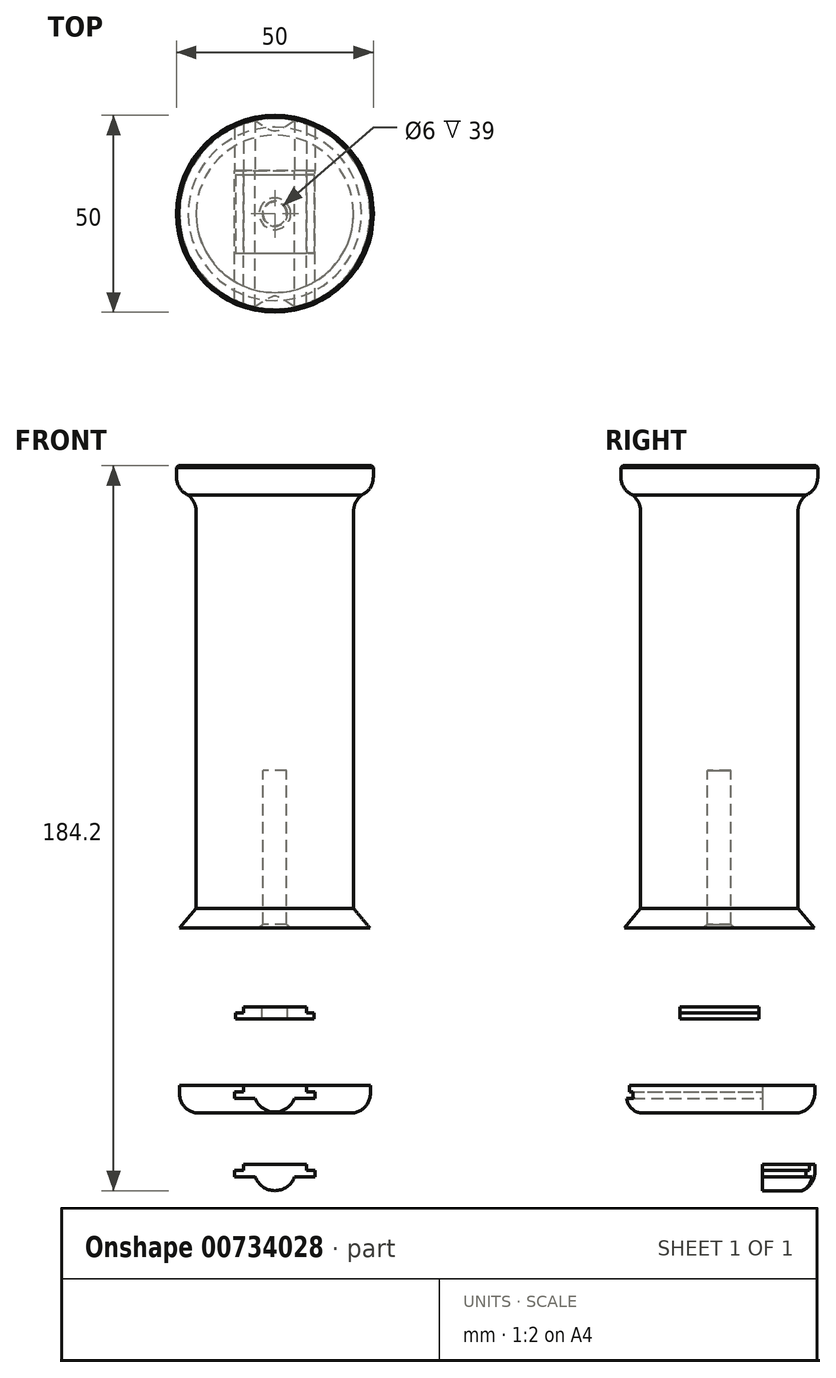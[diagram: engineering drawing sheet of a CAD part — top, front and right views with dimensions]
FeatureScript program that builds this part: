
annotation { "Feature Type Name" : "Feature", "Feature Type Description" : "" }
export const myFeature = defineFeature(function(context is Context, id is Id, definition is map)
    precondition{}
    {
        {
            var Q0;
            Q0=qCreatedBy(makeId("Front.planeOp"),FACE);
            var sketch = newSketch(context, id + "F0", { "sketchPlane" : qUnion([Q0])});
            skLineSegment(sketch, "E0", {"start": v(3, 0) * mm, "end": v(20, 0) * mm});
            skLineSegment(sketch, "E1", {"start": v(20, 0) * mm, "end": v(20, 110) * mm});
            skLineSegment(sketch, "E2", {"start": v(20, 110) * mm, "end": v(25, 110) * mm});
            skLineSegment(sketch, "E3", {"start": v(25, 110) * mm, "end": v(25, 117.5) * mm});
            skLineSegment(sketch, "E4", {"start": v(25, 117.5) * mm, "end": v(0, 117.5) * mm});
            skLineSegment(sketch, "E5", {"start": v(0, 117.5) * mm, "end": v(0, 40) * mm});
            skLineSegment(sketch, "E6", {"start": v(3, 0) * mm, "end": v(3, 40) * mm});
            skLineSegment(sketch, "E7", {"start": v(3, 40) * mm, "end": v(0, 40) * mm});
            skSolve(sketch);
        }
        {
            var Q0;
            Q0=makeQuery(id+"F0.imprint","IMPRINT",FACE,{"disambiguationData":[TD([[makeQuery(id+"F0.imprint","IMPRINT",EDGE,{"derivedFrom":sQuery(id+"F0.wireOp",EDGE,"E0")}),1.0]])]});
            var Q1;
            Q1=sQuery(id+"F0.wireOp",EDGE,"E5");
            revolve(context, id + "F1", {"surfaceOperationType" : NewSurfaceOperationType.NEW, "entities" : qUnion([Q0]), "axis" : qUnion([Q1]), "revolveType" : RevolveType.FULL});
        }
        {
            var Q0;
            Q0=makeQuery(id+"F1.opRevolve","SWEPT_EDGE",EDGE,{"disambiguationData":[OSD([sQuery(id+"F0.wireOp",EDGE,"E1"),sQuery(id+"F0.wireOp",EDGE,"E2")])]});
            chamfer(context, id + "F2", {"entities" : qUnion([Q0]), "width" : 2 * mm, "tangentPropagation" : true});
        }
        {
            var Q0;
            {var subQ0=sQuery(id+"F0.wireOp",EDGE,"E1");Q0=makeQuery(id+"F2.opChamfer","BLEND_EDGE",EDGE,{"blendedFrom":[makeQuery(id+"F1.opRevolve","SWEPT_EDGE",EDGE,{"disambiguationData":[OSD([subQ0,sQuery(id+"F0.wireOp",EDGE,"E2")])]}),makeQuery(id+"F1.opRevolve","SWEPT_FACE",FACE,{"disambiguationData":[OSD([subQ0])]})],"blendedInto":[makeQuery(id+"F1.opRevolve","SWEPT_FACE",FACE,{"disambiguationData":[OSD([subQ0])]})]});}
            var Q1;
            Q1=makeQuery(id+"F1.opRevolve","SWEPT_EDGE",EDGE,{"disambiguationData":[OSD([sQuery(id+"F0.wireOp",EDGE,"E2"),sQuery(id+"F0.wireOp",EDGE,"E3")])]});
            fillet(context, id + "F3", {"entities" : qUnion([Q0, Q1]), "radius" : 5 * mm, "tangentPropagation" : true, "allowEdgeOverflow" : false});
        }
        {
            var Q0;
            Q0=makeQuery(id+"F1.opRevolve","SWEPT_EDGE",EDGE,{"disambiguationData":[OSD([sQuery(id+"F0.wireOp",EDGE,"E0"),sQuery(id+"F0.wireOp",EDGE,"E6")])]});
            chamfer(context, id + "F4", {"entities" : qUnion([Q0]), "width" : 1 * mm, "tangentPropagation" : true});
        }
        {
            var Q0;
            Q0=makeQuery(id+"F1.opRevolve","SWEPT_EDGE",EDGE,{"disambiguationData":[OSD([sQuery(id+"F0.wireOp",EDGE,"E3"),sQuery(id+"F0.wireOp",EDGE,"E4")])]});
            chamfer(context, id + "F5", {"entities" : qUnion([Q0]), "width" : 0.5 * mm, "tangentPropagation" : true});
        }
        {
            var Q0;
            Q0=qCreatedBy(makeId("Top.planeOp"),FACE);
            var sketch = newSketch(context, id + "F6", { "sketchPlane" : qUnion([Q0])});
            skCircle(sketch, "E8", {"center": v(0, 0) * mm, "radius": 25 * mm});
            skCircle(sketch, "E9", {"center": v(0, 0) * mm, "radius": 20 * mm});
            skSolve(sketch);
        }
        {
            var Q0;
            Q0 = qSketchRegion(id + "F6", true);
            extrude(context, id + "F7", {"entities" : qUnion([Q0]), "operationType" : NewBodyOperationType.ADD, "depth" : 5 * mm, "offsetDistance" : 25 * mm});
        }
        {
            var Q0;
            Q0=makeQuery(id+"F7.opExtrude","CAP_EDGE",EDGE,{"disambiguationData":[OSD([sQuery(id+"F6.wireOp",EDGE,"E8")])],"isStart":false});
            chamfer(context, id + "F8", {"entities" : qUnion([Q0]), "chamferType" : ChamferType.TWO_OFFSETS, "width1" : 5 * mm, "oppositeDirection" : false, "width2" : 6 * mm, "tangentPropagation" : true});
        }
        {
            var Q0;
            Q0=qCreatedBy(makeId("Top.planeOp"),FACE);
            cPlane(context, id + "F9", {"entities" : qUnion([Q0]), "cplaneType" : CPlaneType.OFFSET, "offset" : 20 * mm, "oppositeDirection" : true, "width" : 150 * mm, "height" : 150 * mm});
        }
        {
            var Q0;
            Q0=qCreatedBy(id+"F9.planeOp",FACE);
            var sketch = newSketch(context, id + "F10", { "sketchPlane" : qUnion([Q0])});
            skCircle(sketch, "E10", {"center": v(0, 0) * mm, "radius": 3.2 * mm});
            skLineSegment(sketch, "E11.bottom", {"start": v(-10, -10) * mm, "end": v(10, -10) * mm});
            skLineSegment(sketch, "E11.top", {"start": v(-10, 10) * mm, "end": v(10, 10) * mm});
            skLineSegment(sketch, "E11.left", {"start": v(-10, -10) * mm, "end": v(-10, 10) * mm});
            skLineSegment(sketch, "E11.right", {"start": v(10, -10) * mm, "end": v(10, 10) * mm});
            skSolve(sketch);
        }
        {
            var Q0;
            Q0=makeQuery(id+"F10.imprint","IMPRINT",FACE,{"disambiguationData":[TD([[makeQuery(id+"F10.imprint","IMPRINT",EDGE,{"derivedFrom":sQuery(id+"F10.wireOp",EDGE,"E10")}),-1.0]])]});
            extrude(context, id + "F11", {"entities" : qUnion([Q0]), "oppositeDirection" : true, "depth" : 3 * mm, "offsetDistance" : 25 * mm});
        }
        {
            var Q0;
            Q0=qCreatedBy(makeId("Front.planeOp"),FACE);
            var sketch = newSketch(context, id + "F12", { "sketchPlane" : qUnion([Q0])});
            skLineSegment(sketch, "E12.bottom", {"start": v(-10, -20) * mm, "end": v(-8, -20) * mm});
            skLineSegment(sketch, "E12.top", {"start": v(-10, -21.5) * mm, "end": v(-8, -21.5) * mm});
            skLineSegment(sketch, "E12.left", {"start": v(-10, -20) * mm, "end": v(-10, -21.5) * mm});
            skLineSegment(sketch, "E12.right", {"start": v(-8, -20) * mm, "end": v(-8, -21.5) * mm});
            skLineSegment(sketch, "E13", {"start": v(0, -22.98) * mm, "end": v(0, -19.98) * mm});
            skLineSegment(sketch, "E14.MirrorCS", {"start": v(10, -20) * mm, "end": v(10, -21.5) * mm});
            skLineSegment(sketch, "E15.MirrorCS", {"start": v(10, -21.5) * mm, "end": v(8, -21.5) * mm});
            skLineSegment(sketch, "E16.MirrorCS", {"start": v(8, -20) * mm, "end": v(8, -21.5) * mm});
            skLineSegment(sketch, "E17.MirrorCS", {"start": v(10, -20) * mm, "end": v(8, -20) * mm});
            skSolve(sketch);
        }
        {
            var Q0;
            Q0 = qSketchRegion(id + "F12", true);
            extrude(context, id + "F13", {"entities" : qUnion([Q0]), "operationType" : NewBodyOperationType.REMOVE, "endBound" : BoundingType.SYMMETRIC, "oppositeDirection" : true, "depth" : 20 * mm, "offsetDistance" : 25 * mm});
        }
        {
            var Q0;
            Q0=qCreatedBy(id+"F9.planeOp",FACE);
            cPlane(context, id + "F14", {"entities" : qUnion([Q0]), "cplaneType" : CPlaneType.OFFSET, "offset" : 20 * mm, "oppositeDirection" : true, "width" : 150 * mm, "height" : 150 * mm});
        }
        {
            var Q0;
            Q0=qCreatedBy(id+"F14.planeOp",FACE);
            var sketch = newSketch(context, id + "F15", { "sketchPlane" : qUnion([Q0])});
            skCircle(sketch, "E18", {"center": v(0, 0) * mm, "radius": 24.25 * mm});
            skSolve(sketch);
        }
        {
            var Q0;
            Q0=makeQuery(id+"F15.imprint","IMPRINT",FACE,{"disambiguationData":[TD([[makeQuery(id+"F15.imprint","IMPRINT",EDGE,{"derivedFrom":sQuery(id+"F15.wireOp",EDGE,"E18")}),1.0]])]});
            extrude(context, id + "F16", {"entities" : qUnion([Q0]), "oppositeDirection" : true, "depth" : 7 * mm, "offsetDistance" : 25 * mm});
        }
        {
            var Q0;
            Q0=makeQuery(id+"F16.opExtrude","CAP_EDGE",EDGE,{"disambiguationData":[OSD([sQuery(id+"F15.wireOp",EDGE,"E18")])],"isStart":false});
            fillet(context, id + "F17", {"entities" : qUnion([Q0]), "radius" : 5 * mm, "tangentPropagation" : true, "allowEdgeOverflow" : false});
        }
        {
            var Q0;
            Q0=qCreatedBy(makeId("Front.planeOp"),FACE);
            var sketch = newSketch(context, id + "F18", { "sketchPlane" : qUnion([Q0])});
            skLineSegment(sketch, "E19", {"start": v(0, -40) * mm, "end": v(-8, -40) * mm});
            skLineSegment(sketch, "E20", {"start": v(-8, -40) * mm, "end": v(-8, -41.6) * mm});
            skLineSegment(sketch, "E21", {"start": v(-8, -41.6) * mm, "end": v(-10.2, -41.6) * mm});
            skLineSegment(sketch, "E22", {"start": v(-10.2, -41.6) * mm, "end": v(-10.2, -43.2) * mm});
            skLineSegment(sketch, "E23", {"start": v(-10.2, -43.2) * mm, "end": v(0, -43.2) * mm});
            skLineSegment(sketch, "E24", {"start": v(0, -40) * mm, "end": v(0, -43.2) * mm});
            skLineSegment(sketch, "E25.MirrorCS", {"start": v(0, -40) * mm, "end": v(8, -40) * mm});
            skLineSegment(sketch, "E26.MirrorCS", {"start": v(10.2, -41.6) * mm, "end": v(10.2, -43.2) * mm});
            skLineSegment(sketch, "E27.MirrorCS", {"start": v(8, -41.6) * mm, "end": v(10.2, -41.6) * mm});
            skLineSegment(sketch, "E28.MirrorCS", {"start": v(8, -40) * mm, "end": v(8, -41.6) * mm});
            skLineSegment(sketch, "E29.MirrorCS", {"start": v(10.2, -43.2) * mm, "end": v(0, -43.2) * mm});
            skArc(sketch, "E30", {"start": v(-5, -43.2) * mm, "mid": v(0, -46.7) * mm, "end": v(5, -43.2) * mm});
            skSolve(sketch);
        }
        {
            var Q0;
            Q0 = qSketchRegion(id + "F18", true);
            extrude(context, id + "F19", {"entities" : qUnion([Q0]), "operationType" : NewBodyOperationType.REMOVE, "depth" : 25 * mm, "offsetDistance" : 25 * mm});
        }
        {
            var Q0;
            Q0=makeQuery(id+"F19.boolean.opBoolean","COPY",FACE,{"derivedFrom":makeQuery(id+"F19.opExtrude","CAP_FACE",FACE,{"disambiguationData":[OSD([sQuery(id+"F18.wireOp",EDGE,"E19"),sQuery(id+"F18.wireOp",EDGE,"E20"),sQuery(id+"F18.wireOp",EDGE,"E21"),sQuery(id+"F18.wireOp",EDGE,"E22"),sQuery(id+"F18.wireOp",EDGE,"E23"),sQuery(id+"F18.wireOp",EDGE,"E25.MirrorCS"),sQuery(id+"F18.wireOp",EDGE,"E26.MirrorCS"),sQuery(id+"F18.wireOp",EDGE,"E27.MirrorCS"),sQuery(id+"F18.wireOp",EDGE,"E28.MirrorCS"),sQuery(id+"F18.wireOp",EDGE,"E29.MirrorCS")])],"isStart":true})});
            extrude(context, id + "F20", {"entities" : qUnion([Q0]), "operationType" : NewBodyOperationType.REMOVE, "oppositeDirection" : true, "depth" : 11 * mm, "offsetDistance" : 25 * mm});
        }
        {
            var Q0;
            Q0=makeQuery(id+"F16.opExtrude","SWEPT_BODY",BODY,{"disambiguationData":[OSD([sQuery(id+"F15.wireOp",EDGE,"E18")])]});
            transform(context, id + "F21", {"entities" : qUnion([Q0]), "transformType" : TransformType.TRANSLATION_3D, "dx" : 0 * mm, "dy" : 0 * mm, "dz" : -20 * mm, "makeCopy" : true});
        }
        {
            var Q0;
            Q0=makeQuery(id+"F21.opPattern","COPY",FACE,{"derivedFrom":makeQuery(id+"F20.boolean.opBoolean","COPY",FACE,{"derivedFrom":makeQuery(id+"F20.opExtrude","CAP_FACE",FACE,{"disambiguationData":[OSD([sQuery(id+"F18.wireOp",EDGE,"E19"),sQuery(id+"F18.wireOp",EDGE,"E20"),sQuery(id+"F18.wireOp",EDGE,"E21"),sQuery(id+"F18.wireOp",EDGE,"E22"),sQuery(id+"F18.wireOp",EDGE,"E23"),sQuery(id+"F18.wireOp",EDGE,"E25.MirrorCS"),sQuery(id+"F18.wireOp",EDGE,"E26.MirrorCS"),sQuery(id+"F18.wireOp",EDGE,"E27.MirrorCS"),sQuery(id+"F18.wireOp",EDGE,"E28.MirrorCS"),sQuery(id+"F18.wireOp",EDGE,"E29.MirrorCS"),sQuery(id+"F18.wireOp",EDGE,"E30")])],"isStart":false})}),"instanceName":"1"});
            var sketch = newSketch(context, id + "F22", { "sketchPlane" : qUnion([Q0])});
            skLineSegment(sketch, "E31", {"start": v(7.9, -60) * mm, "end": v(7.9, -61.7) * mm});
            skLineSegment(sketch, "E32", {"start": v(7.9, -61.7) * mm, "end": v(10.1, -61.7) * mm});
            skLineSegment(sketch, "E33", {"start": v(10.1, -61.7) * mm, "end": v(10.1, -63.1) * mm});
            skLineSegment(sketch, "E34", {"start": v(10.1, -63.1) * mm, "end": v(4.9, -63.1) * mm});
            skLineSegment(sketch, "E35", {"start": v(0, -60) * mm, "end": v(0, -63.02) * mm});
            skLineSegment(sketch, "E36.MirrorCS", {"start": v(-7.9, -61.7) * mm, "end": v(-10.1, -61.7) * mm});
            skLineSegment(sketch, "E37.MirrorCS", {"start": v(-10.1, -61.7) * mm, "end": v(-10.1, -63.1) * mm});
            skLineSegment(sketch, "E38.MirrorCS", {"start": v(-10.1, -63.1) * mm, "end": v(-4.9, -63.1) * mm});
            skLineSegment(sketch, "E39.MirrorCS", {"start": v(-7.9, -60) * mm, "end": v(-7.9, -61.7) * mm});
            skArc(sketch, "E40", {"start": v(-4.9, -63.1) * mm, "mid": v(0, -66.56) * mm, "end": v(4.9, -63.1) * mm});
            skLineSegment(sketch, "E41", {"start": v(7.9, -60) * mm, "end": v(31.99, -60) * mm});
            skLineSegment(sketch, "E42", {"start": v(31.99, -60) * mm, "end": v(31.99, -71.03) * mm});
            skLineSegment(sketch, "E43", {"start": v(31.99, -71.03) * mm, "end": v(-32.2, -71.03) * mm});
            skLineSegment(sketch, "E44", {"start": v(-32.2, -71.03) * mm, "end": v(-32.2, -60) * mm});
            skLineSegment(sketch, "E45", {"start": v(-32.2, -60) * mm, "end": v(-7.9, -60) * mm});
            skSolve(sketch);
        }
        {
            var Q0;
            {var subQ5=sQuery(id+"F22.wireOp",EDGE,"E42");Q0=makeQuery(id+"F22.imprint","IMPRINT",FACE,{"disambiguationData":[TD([[makeQuery(id+"F22.imprint","IMPRINT",EDGE,{"derivedFrom":subQ5}),-1.0]])]});}
            extrude(context, id + "F23", {"entities" : qUnion([Q0]), "operationType" : NewBodyOperationType.REMOVE, "endBound" : BoundingType.SYMMETRIC, "oppositeDirection" : true, "depth" : 100 * mm, "offsetDistance" : 25 * mm});
        }
    });
